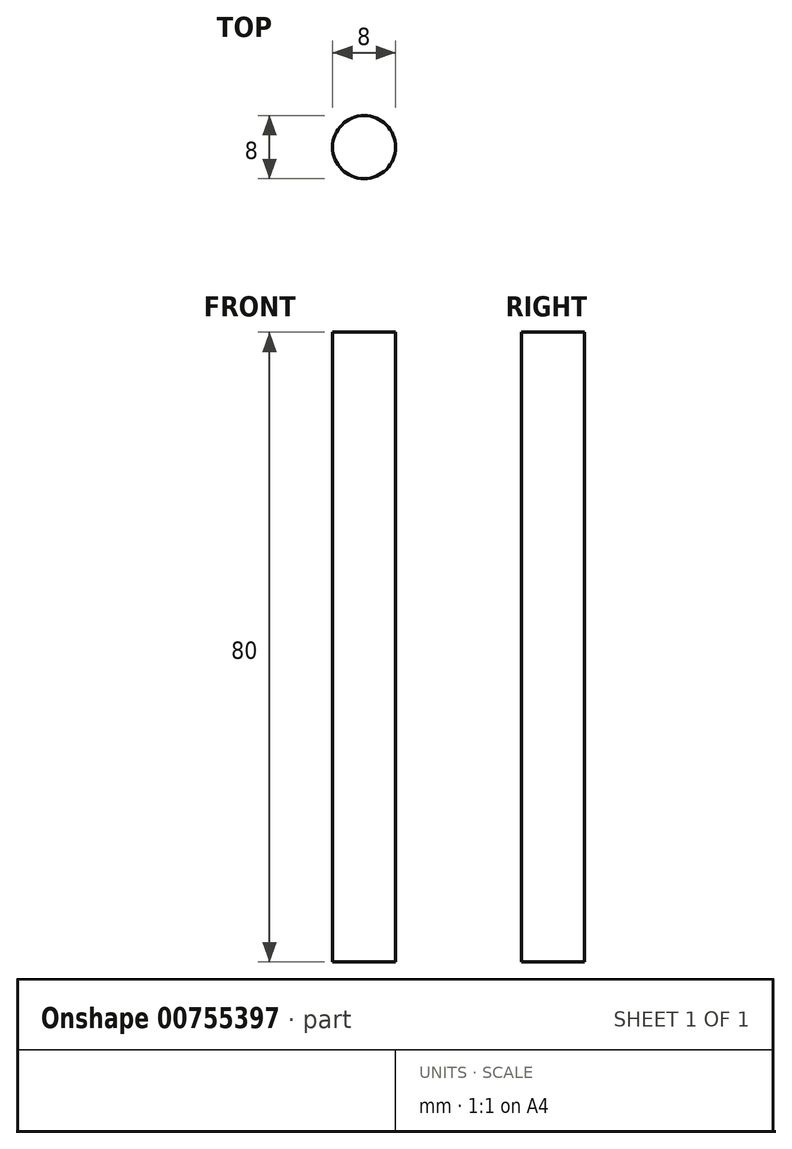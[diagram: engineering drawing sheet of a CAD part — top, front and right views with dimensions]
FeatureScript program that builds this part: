
annotation { "Feature Type Name" : "Feature", "Feature Type Description" : "" }
export const myFeature = defineFeature(function(context is Context, id is Id, definition is map)
    precondition{}
    {
        {
            var Q0;
            Q0=qCreatedBy(makeId("Top.planeOp"),FACE);
            var sketch = newSketch(context, id + "F0", { "sketchPlane" : qUnion([Q0])});
            skCircle(sketch, "E0", {"center": v(0, 0) * mm, "radius": 4 * mm});
            skSolve(sketch);
        }
        {
            var Q0;
            Q0 = qSketchRegion(id + "F0", true);
            extrude(context, id + "F1", {"entities" : qUnion([Q0]), "depth" : 80 * mm, "offsetDistance" : 25 * mm});
        }
    });
